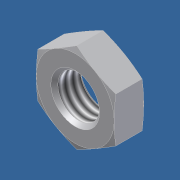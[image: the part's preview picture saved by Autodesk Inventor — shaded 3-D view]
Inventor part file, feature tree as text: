
AUTODESK INVENTOR PART (.ipt)
format: ipt  version: 2012 (Build 160160000, 160)  size: 129,536 bytes
history: native  units: in
note: dims shown in document units (in); Inventor stores cm internally (conversion verified against a paired STEP export)
features: other x70, sketch x3, revolve x2, extrude x1, thread x1
ambient origin geometry x8: Origin, YZ Plane, XZ Plane, XY Plane, X Axis, Y Axis, Z Axis, Center Point
bodies: Solid1 (feature_tree)
feature tree (77):
  sketch  "Sketch_8"  dims[d0=360.0deg d1=0.19in d2=0.0in]
  sketch  "Sketch_10"  dims[d3=360.0deg d4=0.19in d5=0.0in]
  revolve  "Revolution1"  [1 undecoded]
  extrude  "Extrusion1"  Depth=0.19in TaperAngle=0.0deg
  revolve  "Revolution2"  [1 undecoded]
  thread  "Thread1"  [1 undecoded]
  other  "NUT_XY"
  other  "NUT_YZ"
  other  "NUT_ZX"
  other  "NUT_X"
  other  "NUT_Y"
  other  "NUT_Z"
  other  "NUT_Center"
  other  "a1_XY"
  other  "a1_YZ"
  other  "a1_ZX"
  other  "a1_X"
  other  "a1_Y"
  other  "a1_Z"
  other  "a1_Center"
  other  "a2_XY"
  other  "a2_YZ"
  other  "a2_ZX"
  other  "a2_X"
  other  "a2_Y"
  other  "a2_Z"
  other  "a2_Center"
  other  "b1_XY"
  other  "b1_YZ"
  other  "b1_ZX"
  other  "b1_X"
  other  "b1_Y"
  other  "b1_Z"
  other  "b1_Center"
  other  "b2_XY"
  other  "b2_YZ"
  other  "b2_ZX"
  other  "b2_X"
  other  "b2_Y"
  other  "b2_Z"
  other  "b2_Center"
  other  "e_XY"
  other  "e_YZ"
  other  "e_ZX"
  other  "e_X"
  other  "e_Y"
  other  "e_Z"
  other  "e_Center"
  other  "th1_XY"
  other  "th1_YZ"
  other  "th1_ZX"
  other  "th1_X"
  other  "th1_Y"
  other  "th1_Z"
  other  "th1_Center"
  other  "th2_XY"
  other  "th2_YZ"
  other  "th2_ZX"
  other  "th2_X"
  other  "th2_Y"
  other  "th2_Z"
  other  "th2_Center"
  other  "ol1_XY"
  other  "ol1_YZ"
  other  "ol1_ZX"
  other  "ol1_X"
  other  "ol1_Y"
  other  "ol1_Z"
  other  "ol1_Center"
  other  "ol2_XY"
  other  "ol2_YZ"
  other  "ol2_ZX"
  other  "ol2_X"
  other  "ol2_Y"
  other  "ol2_Z"
  other  "ol2_Center"
  sketch  "Sketch_11"
note: 3 required parameter values undecoded (feature->parameter linkage not recoverable at this tier; creation-order binding heuristic only, values carry confidence <= 0.55)